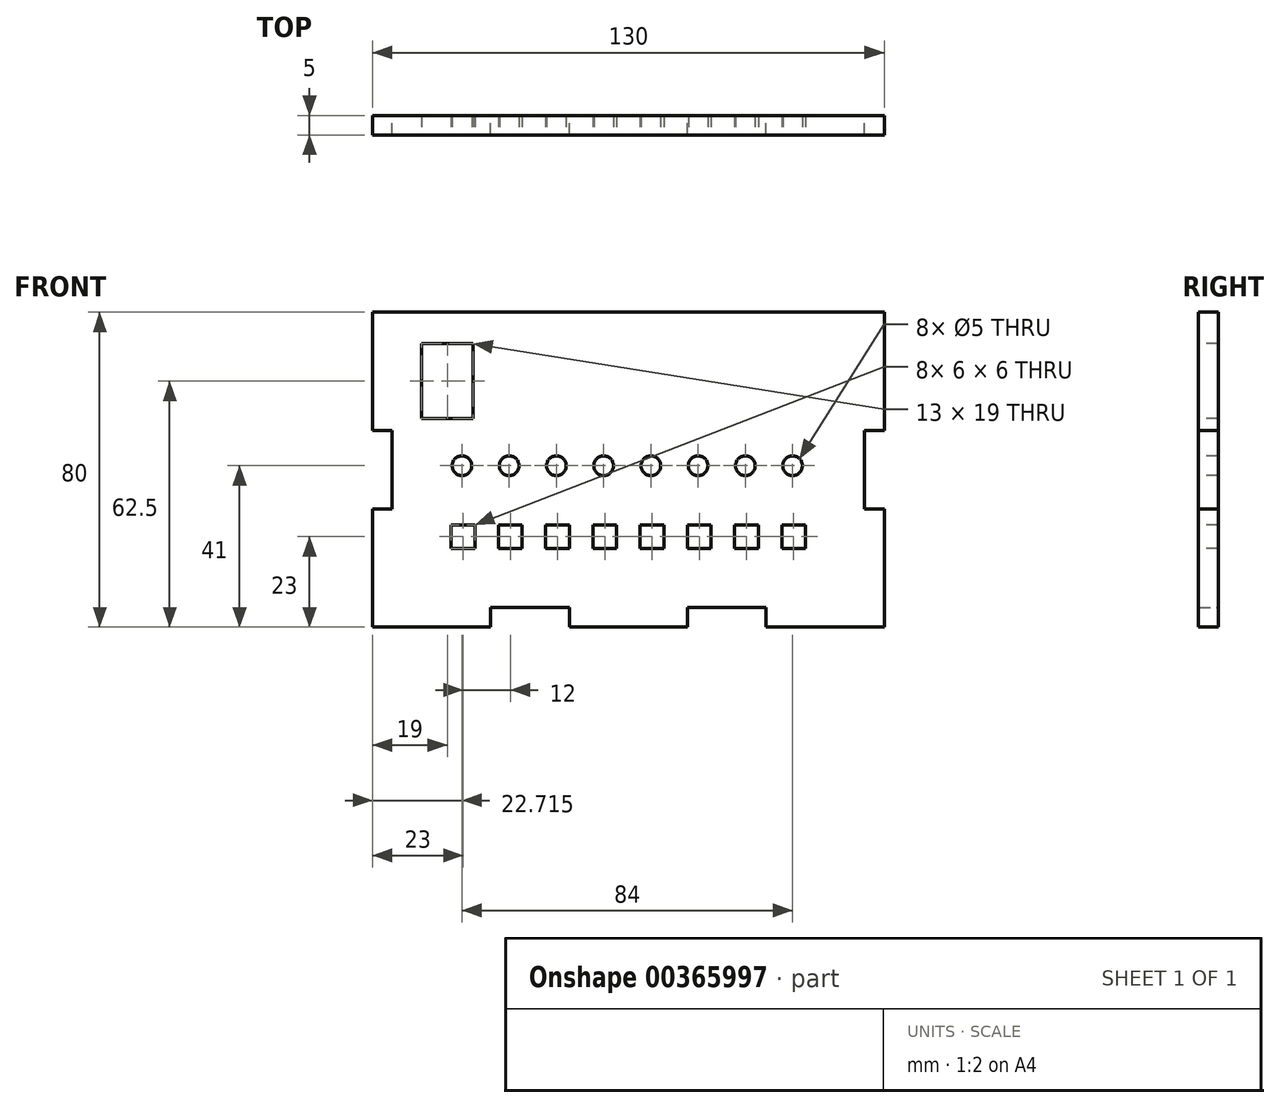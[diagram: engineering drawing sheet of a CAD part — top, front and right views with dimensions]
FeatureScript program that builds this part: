
annotation { "Feature Type Name" : "Feature", "Feature Type Description" : "" }
export const myFeature = defineFeature(function(context is Context, id is Id, definition is map)
    precondition{}
    {
        {
            var Q0;
            Q0=qCreatedBy(makeId("Front.planeOp"),FACE);
            var sketch = newSketch(context, id + "F0", { "sketchPlane" : qUnion([Q0])});
            skLineSegment(sketch, "E0", {"start": v(0, 0) * mm, "end": v(30, 0) * mm});
            skLineSegment(sketch, "E1", {"start": v(30, 0) * mm, "end": v(30, 5) * mm});
            skLineSegment(sketch, "E2", {"start": v(30, 5) * mm, "end": v(50, 5) * mm});
            skLineSegment(sketch, "E3", {"start": v(50, 5) * mm, "end": v(50, 0) * mm});
            skLineSegment(sketch, "E4", {"start": v(50, 0) * mm, "end": v(80, 0) * mm});
            skLineSegment(sketch, "E5", {"start": v(80, 0) * mm, "end": v(80, 5) * mm});
            skLineSegment(sketch, "E6", {"start": v(80, 5) * mm, "end": v(100, 5) * mm});
            skLineSegment(sketch, "E7", {"start": v(100, 5) * mm, "end": v(100, 0) * mm});
            skLineSegment(sketch, "E8", {"start": v(100, 0) * mm, "end": v(130, 0) * mm});
            skLineSegment(sketch, "E9", {"start": v(130, 0) * mm, "end": v(130, 30) * mm});
            skLineSegment(sketch, "E10", {"start": v(130, 30) * mm, "end": v(125, 30) * mm});
            skLineSegment(sketch, "E11", {"start": v(125, 30) * mm, "end": v(125, 50) * mm});
            skLineSegment(sketch, "E12", {"start": v(125, 50) * mm, "end": v(130, 50) * mm});
            skLineSegment(sketch, "E13", {"start": v(130, 50) * mm, "end": v(130, 80) * mm});
            skLineSegment(sketch, "E14", {"start": v(130, 80) * mm, "end": v(0, 80) * mm});
            skLineSegment(sketch, "E15", {"start": v(0, 80) * mm, "end": v(0, 50) * mm});
            skLineSegment(sketch, "E16", {"start": v(0, 50) * mm, "end": v(5, 50) * mm});
            skLineSegment(sketch, "E17", {"start": v(5, 50) * mm, "end": v(5, 30) * mm});
            skLineSegment(sketch, "E18", {"start": v(5, 30) * mm, "end": v(0, 30) * mm});
            skLineSegment(sketch, "E19", {"start": v(0, 30) * mm, "end": v(0, 0) * mm});
            skSolve(sketch);
        }
        {
            var Q0;
            Q0=makeQuery(id+"F0.imprint","IMPRINT",FACE,{"disambiguationData":[TD([[makeQuery(id+"F0.imprint","IMPRINT",EDGE,{"derivedFrom":sQuery(id+"F0.wireOp",EDGE,"E0")}),1.0]])]});
            extrude(context, id + "F1", {"entities" : qUnion([Q0]), "depth" : 5 * mm});
        }
        {
            var Q0;
            Q0=makeQuery(id+"F1.opExtrude","CAP_FACE",FACE,{"disambiguationData":[OSD([sQuery(id+"F0.wireOp",EDGE,"E0"),sQuery(id+"F0.wireOp",EDGE,"E1"),sQuery(id+"F0.wireOp",EDGE,"E2"),sQuery(id+"F0.wireOp",EDGE,"E3"),sQuery(id+"F0.wireOp",EDGE,"E4"),sQuery(id+"F0.wireOp",EDGE,"E5"),sQuery(id+"F0.wireOp",EDGE,"E6"),sQuery(id+"F0.wireOp",EDGE,"E7"),sQuery(id+"F0.wireOp",EDGE,"E8"),sQuery(id+"F0.wireOp",EDGE,"E9"),sQuery(id+"F0.wireOp",EDGE,"E10"),sQuery(id+"F0.wireOp",EDGE,"E11"),sQuery(id+"F0.wireOp",EDGE,"E12"),sQuery(id+"F0.wireOp",EDGE,"E13"),sQuery(id+"F0.wireOp",EDGE,"E14"),sQuery(id+"F0.wireOp",EDGE,"E15"),sQuery(id+"F0.wireOp",EDGE,"E16"),sQuery(id+"F0.wireOp",EDGE,"E17"),sQuery(id+"F0.wireOp",EDGE,"E18"),sQuery(id+"F0.wireOp",EDGE,"E19")])],"isStart":false});
            var sketch = newSketch(context, id + "F2", { "sketchPlane" : qUnion([Q0])});
            skLineSegment(sketch, "E20.bottom", {"start": v(12.5, 72) * mm, "end": v(25.5, 72) * mm});
            skLineSegment(sketch, "E20.top", {"start": v(12.5, 53) * mm, "end": v(25.5, 53) * mm});
            skLineSegment(sketch, "E20.left", {"start": v(12.5, 72) * mm, "end": v(12.5, 53) * mm});
            skLineSegment(sketch, "E20.right", {"start": v(25.5, 72) * mm, "end": v(25.5, 53) * mm});
            skLineSegment(sketch, "E21.bottom", {"start": v(32, 26) * mm, "end": v(38, 26) * mm});
            skLineSegment(sketch, "E21.top", {"start": v(32, 20) * mm, "end": v(38, 20) * mm});
            skLineSegment(sketch, "E21.left", {"start": v(32, 26) * mm, "end": v(32, 20) * mm});
            skLineSegment(sketch, "E21.right", {"start": v(38, 26) * mm, "end": v(38, 20) * mm});
            skLineSegment(sketch, "E22.bottom", {"start": v(50, 20) * mm, "end": v(44, 20) * mm});
            skLineSegment(sketch, "E22.top", {"start": v(50, 26) * mm, "end": v(44, 26) * mm});
            skLineSegment(sketch, "E22.left", {"start": v(50, 20) * mm, "end": v(50, 26) * mm});
            skLineSegment(sketch, "E22.right", {"start": v(44, 20) * mm, "end": v(44, 26) * mm});
            skPoint(sketch, "E22.middle", {"position": v(47, 23) * mm});
            skLineSegment(sketch, "E23.bottom", {"start": v(62, 20) * mm, "end": v(56, 20) * mm});
            skLineSegment(sketch, "E23.top", {"start": v(62, 26) * mm, "end": v(56, 26) * mm});
            skLineSegment(sketch, "E23.left", {"start": v(62, 20) * mm, "end": v(62, 26) * mm});
            skLineSegment(sketch, "E23.right", {"start": v(56, 20) * mm, "end": v(56, 26) * mm});
            skLineSegment(sketch, "E24.bottom", {"start": v(74, 20) * mm, "end": v(68, 20) * mm});
            skLineSegment(sketch, "E24.top", {"start": v(74, 26) * mm, "end": v(68, 26) * mm});
            skLineSegment(sketch, "E24.left", {"start": v(74, 20) * mm, "end": v(74, 26) * mm});
            skLineSegment(sketch, "E24.right", {"start": v(68, 20) * mm, "end": v(68, 26) * mm});
            skLineSegment(sketch, "E25.bottom", {"start": v(86, 20) * mm, "end": v(80, 20) * mm});
            skLineSegment(sketch, "E25.top", {"start": v(86, 26) * mm, "end": v(80, 26) * mm});
            skLineSegment(sketch, "E25.left", {"start": v(86, 20) * mm, "end": v(86, 26) * mm});
            skLineSegment(sketch, "E25.right", {"start": v(80, 20) * mm, "end": v(80, 26) * mm});
            skLineSegment(sketch, "E26.bottom", {"start": v(98, 20) * mm, "end": v(92, 20) * mm});
            skLineSegment(sketch, "E26.top", {"start": v(98, 26) * mm, "end": v(92, 26) * mm});
            skLineSegment(sketch, "E26.left", {"start": v(98, 20) * mm, "end": v(98, 26) * mm});
            skLineSegment(sketch, "E26.right", {"start": v(92, 20) * mm, "end": v(92, 26) * mm});
            skLineSegment(sketch, "E27.bottom", {"start": v(110, 20) * mm, "end": v(104, 20) * mm});
            skLineSegment(sketch, "E27.top", {"start": v(110, 26) * mm, "end": v(104, 26) * mm});
            skLineSegment(sketch, "E27.left", {"start": v(110, 20) * mm, "end": v(110, 26) * mm});
            skLineSegment(sketch, "E27.right", {"start": v(104, 20) * mm, "end": v(104, 26) * mm});
            skLineSegment(sketch, "E28.bottom", {"start": v(26, 20) * mm, "end": v(20, 20) * mm});
            skLineSegment(sketch, "E28.top", {"start": v(26, 26) * mm, "end": v(20, 26) * mm});
            skLineSegment(sketch, "E28.left", {"start": v(26, 20) * mm, "end": v(26, 26) * mm});
            skLineSegment(sketch, "E28.right", {"start": v(20, 20) * mm, "end": v(20, 26) * mm});
            skCircle(sketch, "E29", {"center": v(22.71, 41) * mm, "radius": 2.5 * mm});
            skCircle(sketch, "E30", {"center": v(34.71, 41) * mm, "radius": 2.5 * mm});
            skCircle(sketch, "E31", {"center": v(46.71, 41) * mm, "radius": 2.5 * mm});
            skCircle(sketch, "E32", {"center": v(58.71, 41) * mm, "radius": 2.5 * mm});
            skCircle(sketch, "E33", {"center": v(70.71, 41) * mm, "radius": 2.5 * mm});
            skCircle(sketch, "E34", {"center": v(82.71, 41) * mm, "radius": 2.5 * mm});
            skCircle(sketch, "E35", {"center": v(94.71, 41) * mm, "radius": 2.5 * mm});
            skCircle(sketch, "E36", {"center": v(106.71, 41) * mm, "radius": 2.5 * mm});
            skSolve(sketch);
        }
        {
            var Q0;
            Q0=makeQuery(id+"F2.imprint","IMPRINT",FACE,{"disambiguationData":[TD([[makeQuery(id+"F2.imprint","IMPRINT",EDGE,{"derivedFrom":sQuery(id+"F2.wireOp",EDGE,"E20.bottom")}),-1.0]])]});
            var Q1;
            Q1=makeQuery(id+"F2.imprint","IMPRINT",FACE,{"disambiguationData":[TD([[makeQuery(id+"F2.imprint","IMPRINT",EDGE,{"derivedFrom":sQuery(id+"F2.wireOp",EDGE,"E29")}),1.0]])]});
            var Q2;
            Q2=makeQuery(id+"F2.imprint","IMPRINT",FACE,{"disambiguationData":[TD([[makeQuery(id+"F2.imprint","IMPRINT",EDGE,{"derivedFrom":sQuery(id+"F2.wireOp",EDGE,"E30")}),1.0]])]});
            var Q3;
            Q3=makeQuery(id+"F2.imprint","IMPRINT",FACE,{"disambiguationData":[TD([[makeQuery(id+"F2.imprint","IMPRINT",EDGE,{"derivedFrom":sQuery(id+"F2.wireOp",EDGE,"E31")}),1.0]])]});
            var Q4;
            Q4=makeQuery(id+"F2.imprint","IMPRINT",FACE,{"disambiguationData":[TD([[makeQuery(id+"F2.imprint","IMPRINT",EDGE,{"derivedFrom":sQuery(id+"F2.wireOp",EDGE,"E32")}),1.0]])]});
            var Q5;
            Q5=makeQuery(id+"F2.imprint","IMPRINT",FACE,{"disambiguationData":[TD([[makeQuery(id+"F2.imprint","IMPRINT",EDGE,{"derivedFrom":sQuery(id+"F2.wireOp",EDGE,"E33")}),1.0]])]});
            var Q6;
            Q6=makeQuery(id+"F2.imprint","IMPRINT",FACE,{"disambiguationData":[TD([[makeQuery(id+"F2.imprint","IMPRINT",EDGE,{"derivedFrom":sQuery(id+"F2.wireOp",EDGE,"E34")}),1.0]])]});
            var Q7;
            Q7=makeQuery(id+"F2.imprint","IMPRINT",FACE,{"disambiguationData":[TD([[makeQuery(id+"F2.imprint","IMPRINT",EDGE,{"derivedFrom":sQuery(id+"F2.wireOp",EDGE,"E35")}),1.0]])]});
            var Q8;
            Q8=makeQuery(id+"F2.imprint","IMPRINT",FACE,{"disambiguationData":[TD([[makeQuery(id+"F2.imprint","IMPRINT",EDGE,{"derivedFrom":sQuery(id+"F2.wireOp",EDGE,"E36")}),1.0]])]});
            var Q9;
            Q9=makeQuery(id+"F2.imprint","IMPRINT",FACE,{"disambiguationData":[TD([[makeQuery(id+"F2.imprint","IMPRINT",EDGE,{"derivedFrom":sQuery(id+"F2.wireOp",EDGE,"E27.bottom")}),-1.0]])]});
            var Q10;
            Q10=makeQuery(id+"F2.imprint","IMPRINT",FACE,{"disambiguationData":[TD([[makeQuery(id+"F2.imprint","IMPRINT",EDGE,{"derivedFrom":sQuery(id+"F2.wireOp",EDGE,"E26.bottom")}),-1.0]])]});
            var Q11;
            Q11=makeQuery(id+"F2.imprint","IMPRINT",FACE,{"disambiguationData":[TD([[makeQuery(id+"F2.imprint","IMPRINT",EDGE,{"derivedFrom":sQuery(id+"F2.wireOp",EDGE,"E25.bottom")}),-1.0]])]});
            var Q12;
            Q12=makeQuery(id+"F2.imprint","IMPRINT",FACE,{"disambiguationData":[TD([[makeQuery(id+"F2.imprint","IMPRINT",EDGE,{"derivedFrom":sQuery(id+"F2.wireOp",EDGE,"E24.bottom")}),-1.0]])]});
            var Q13;
            Q13=makeQuery(id+"F2.imprint","IMPRINT",FACE,{"disambiguationData":[TD([[makeQuery(id+"F2.imprint","IMPRINT",EDGE,{"derivedFrom":sQuery(id+"F2.wireOp",EDGE,"E23.bottom")}),-1.0]])]});
            var Q14;
            Q14=makeQuery(id+"F2.imprint","IMPRINT",FACE,{"disambiguationData":[TD([[makeQuery(id+"F2.imprint","IMPRINT",EDGE,{"derivedFrom":sQuery(id+"F2.wireOp",EDGE,"E22.bottom")}),-1.0]])]});
            var Q15;
            Q15=makeQuery(id+"F2.imprint","IMPRINT",FACE,{"disambiguationData":[TD([[makeQuery(id+"F2.imprint","IMPRINT",EDGE,{"derivedFrom":sQuery(id+"F2.wireOp",EDGE,"E21.bottom")}),-1.0]])]});
            var Q16;
            Q16=makeQuery(id+"F2.imprint","IMPRINT",FACE,{"disambiguationData":[TD([[makeQuery(id+"F2.imprint","IMPRINT",EDGE,{"derivedFrom":sQuery(id+"F2.wireOp",EDGE,"E28.bottom")}),-1.0]])]});
            extrude(context, id + "F3", {"entities" : qUnion([Q0, Q1, Q2, Q3, Q4, Q5, Q6, Q7, Q8, Q9, Q10, Q11, Q12, Q13, Q14, Q15, Q16]), "operationType" : NewBodyOperationType.REMOVE, "oppositeDirection" : true, "depth" : 25 * mm});
        }
    });
